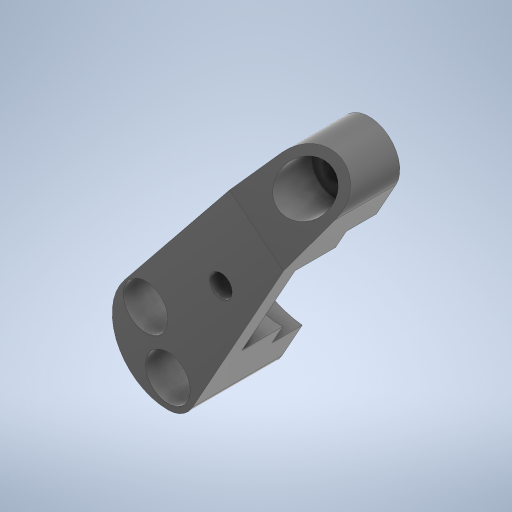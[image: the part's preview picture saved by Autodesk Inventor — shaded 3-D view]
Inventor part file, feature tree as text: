
AUTODESK INVENTOR PART (.ipt)
format: ipt  version: 2023 (Build 270158000, 158)  size: 356,864 bytes
history: native  units: mm
features: extrude x5, sketch x5
ambient origin geometry x8: Origin, YZ Plane, XZ Plane, XY Plane, X Axis, Y Axis, Z Axis, Center Point
bodies: Solid1 (feature_tree)
feature tree (10):
  extrude  "Extrusion1"  Depth=24.0mm
  extrude  "Extrusion2"  Depth=3.0mm
  extrude  "Extrusion3"  Depth=2.1mm
  extrude  "Extrusion4"  Depth=2.5mm
  extrude  "Extrusion5"  Depth=10.0mm
  sketch  "Sketch1"  dims[d0=18.0mm d1=24.0mm]
  sketch  "Sketch3"  dims[d2=2.1mm d3=3.0mm]
  sketch  "Sketch5"  dims[d4=3.0mm d5=2.1mm]
  sketch  "Sketch6"  dims[d6=2.1mm d7=2.5mm]
  sketch  "Sketch8"  dims[d8=5.0mm d9=3.0mm d10=7.0mm d12=10.0mm d15=6.0mm d16=8.0mm d17=0.0mm d18=2.0mm d25=5.5mm d26=10.0mm d27=14.9mm d28=2.7mm d29=0.0mm d30=12.0mm d31=8.251mm d32=4.0mm d33=4.0mm d34=4.0mm d35=4.9mm d36=0.0mm d37=11.4mm d38=3.65mm d39=0.0mm d40=10.0mm d41=0.0mm]
